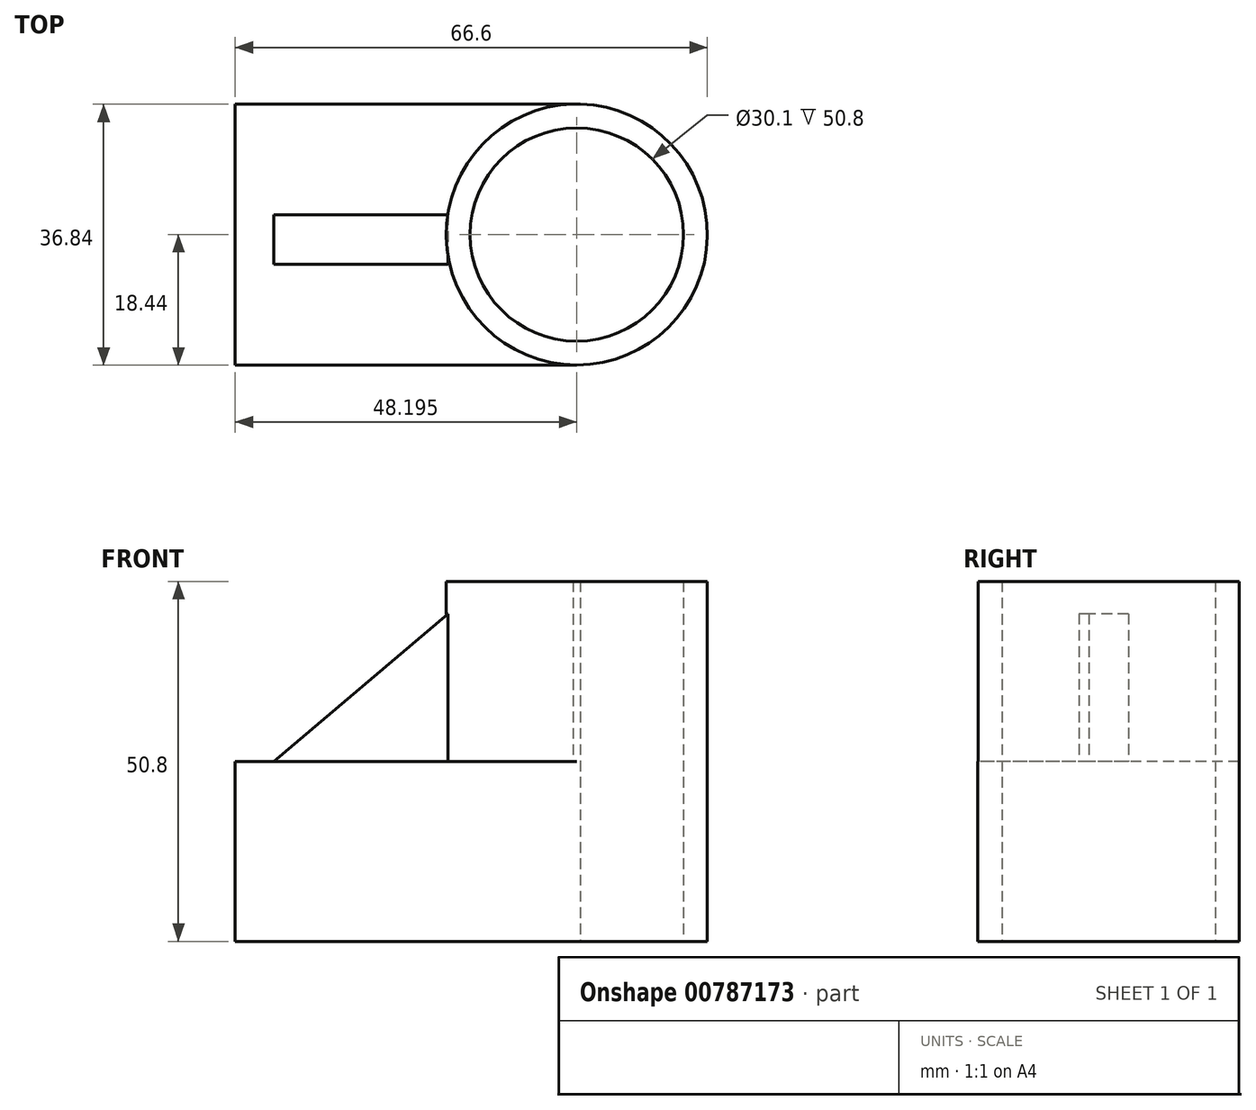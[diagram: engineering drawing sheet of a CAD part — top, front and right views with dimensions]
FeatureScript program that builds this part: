
annotation { "Feature Type Name" : "Feature", "Feature Type Description" : "" }
export const myFeature = defineFeature(function(context is Context, id is Id, definition is map)
    precondition{}
    {
        {
            var Q0;
            Q0=qCreatedBy(makeId("Top.planeOp"),FACE);
            var sketch = newSketch(context, id + "F0", { "sketchPlane" : qUnion([Q0])});
            skCircle(sketch, "E0", {"center": v(18.2, 0) * mm, "radius": 18.4 * mm});
            skCircle(sketch, "E1", {"center": v(18.2, 0) * mm, "radius": 15.05 * mm});
            skLineSegment(sketch, "E2.bottom", {"start": v(18.7, 18.4) * mm, "end": v(-30, 18.4) * mm});
            skLineSegment(sketch, "E2.right", {"start": v(-30, 18.4) * mm, "end": v(-30, -18.44) * mm});
            skLineSegment(sketch, "E3", {"start": v(-30, -18.44) * mm, "end": v(18.2, -18.4) * mm});
            skSolve(sketch);
        }
        {
            var Q0;
            {var subQ4=sQuery(id+"F0.wireOp",EDGE,"E2.right");Q0=makeQuery(id+"F0.imprint","IMPRINT",FACE,{"disambiguationData":[TD([[makeQuery(id+"F0.imprint","IMPRINT",EDGE,{"derivedFrom":subQ4}),1.0]])]});}
            extrude(context, id + "F1", {"entities" : qUnion([Q0]), "depth" : 25.4 * mm, "offsetDistance" : 25.4 * mm});
        }
        {
            var Q0;
            Q0=makeQuery(id+"F0.imprint","IMPRINT",FACE,{"disambiguationData":[TD([[makeQuery(id+"F0.imprint","IMPRINT",EDGE,{"derivedFrom":sQuery(id+"F0.wireOp",EDGE,"E1")}),-1.0]])]});
            extrude(context, id + "F2", {"entities" : qUnion([Q0]), "operationType" : NewBodyOperationType.ADD, "depth" : 50.8 * mm, "offsetDistance" : 25.4 * mm});
        }
        {
            var Q0;
            Q0=makeQuery(id+"F1.opExtrude","CAP_FACE",FACE,{"disambiguationData":[OSD([sQuery(id+"F0.wireOp",EDGE,"E0"),sQuery(id+"F0.wireOp",EDGE,"E2.bottom"),sQuery(id+"F0.wireOp",EDGE,"E2.right"),sQuery(id+"F0.wireOp",EDGE,"E3")])],"isStart":false});
            var sketch = newSketch(context, id + "F3", { "sketchPlane" : qUnion([Q0])});
            skLineSegment(sketch, "E4.bottom", {"start": v(0, 2.8) * mm, "end": v(-24.55, 2.8) * mm});
            skLineSegment(sketch, "E4.top", {"start": v(0, -4.17) * mm, "end": v(-24.55, -4.17) * mm});
            skLineSegment(sketch, "E4.left", {"start": v(0, 2.8) * mm, "end": v(0, -4.17) * mm});
            skLineSegment(sketch, "E4.right", {"start": v(-24.55, 2.8) * mm, "end": v(-24.55, -4.17) * mm});
            skSolve(sketch);
        }
        {
            var Q0;
            {var subQ4=sQuery(id+"F3.wireOp",EDGE,"E4.bottom");Q0=makeQuery(id+"F3.imprint","IMPRINT",FACE,{"disambiguationData":[TD([[makeQuery(id+"F3.imprint","IMPRINT",EDGE,{"derivedFrom":subQ4}),1.0]])]});}
            extrude(context, id + "F4", {"entities" : qUnion([Q0]), "operationType" : NewBodyOperationType.ADD, "depth" : 20.83 * mm, "offsetDistance" : 25.4 * mm});
        }
        {
            var Q0;
            Q0=makeQuery(id+"F4.opExtrude","SWEPT_FACE",FACE,{"disambiguationData":[OSD([sQuery(id+"F3.wireOp",EDGE,"E4.top")])]});
            var sketch = newSketch(context, id + "F5", { "sketchPlane" : qUnion([Q0])});
            skLineSegment(sketch, "E5", {"start": v(0, 46.23) * mm, "end": v(-24.55, 25.4) * mm});
            skSolve(sketch);
        }
        {
            var Q0;
            Q0=makeQuery(id+"F5.imprint","IMPRINT",FACE,{"disambiguationData":[TD([[makeQuery(id+"F5.imprint","IMPRINT",EDGE,{"derivedFrom":sQuery(id+"F5.wireOp",EDGE,"E5")}),-1.0]])]});
            extrude(context, id + "F6", {"entities" : qUnion([Q0]), "operationType" : NewBodyOperationType.REMOVE, "oppositeDirection" : true, "depth" : 25.4 * mm, "offsetDistance" : 25.4 * mm});
        }
    });
